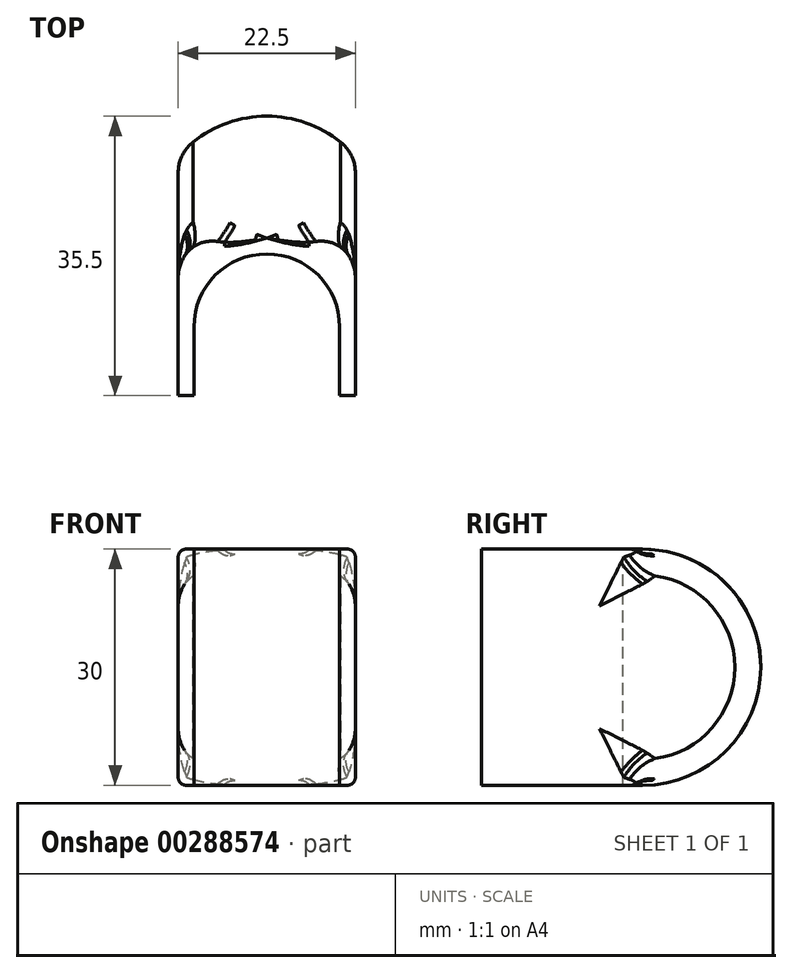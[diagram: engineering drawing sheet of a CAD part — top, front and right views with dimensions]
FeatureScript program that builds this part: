
annotation { "Feature Type Name" : "Feature", "Feature Type Description" : "" }
export const myFeature = defineFeature(function(context is Context, id is Id, definition is map)
    precondition{}
    {
        {
            var Q0;
            Q0=qCreatedBy(makeId("Top.planeOp"),FACE);
            var sketch = newSketch(context, id + "F0", { "sketchPlane" : qUnion([Q0])});
            skLineSegment(sketch, "E0.bottom", {"start": v(11.25, 10) * mm, "end": v(-11.25, 10) * mm});
            skLineSegment(sketch, "E0.top", {"start": v(11.25, -10) * mm, "end": v(-11.25, -10) * mm});
            skLineSegment(sketch, "E0.left", {"start": v(11.25, 10) * mm, "end": v(11.25, -10) * mm});
            skLineSegment(sketch, "E0.right", {"start": v(-11.25, 10) * mm, "end": v(-11.25, -10) * mm});
            skPoint(sketch, "E0.middle", {"position": v(0, 0) * mm});
            skLineSegment(sketch, "E1.bottom", {"start": v(-9.25, -10) * mm, "end": v(9.25, -10) * mm});
            skLineSegment(sketch, "E1.top", {"start": v(-9.25, 8) * mm, "end": v(9.25, 8) * mm});
            skLineSegment(sketch, "E1.left", {"start": v(-9.25, -10) * mm, "end": v(-9.25, 8) * mm});
            skLineSegment(sketch, "E1.right", {"start": v(9.25, -10) * mm, "end": v(9.25, 8) * mm});
            skSolve(sketch);
        }
        {
            var Q0;
            Q0=makeQuery(id+"F0.imprint","IMPRINT",FACE,{"disambiguationData":[TD([[makeQuery(id+"F0.imprint","IMPRINT",EDGE,{"derivedFrom":sQuery(id+"F0.wireOp",EDGE,"E0.bottom")}),1.0]])]});
            extrude(context, id + "F1", {"entities" : qUnion([Q0]), "endBound" : BoundingType.SYMMETRIC, "depth" : 30 * mm, "offsetDistance" : 25 * mm});
        }
        {
            var Q0;
            Q0=makeQuery(id+"F1.opExtrude","SWEPT_FACE",FACE,{"disambiguationData":[OSD([sQuery(id+"F0.wireOp",EDGE,"E0.bottom")])]});
            var sketch = newSketch(context, id + "F2", { "sketchPlane" : qUnion([Q0])});
            skCircle(sketch, "E2", {"center": v(0, 0) * mm, "radius": 15 * mm});
            skSolve(sketch);
        }
        {
            var Q0;
            {var subQ0=sQuery(id+"F2.wireOp",EDGE,"E2");var subQ1=sQuery(id+"F0.wireOp",EDGE,"E0.bottom");var subQ7=makeQuery(id+"F2.imprint","INTERSECT",VERTEX,{"derivedFrom":[makeQuery(id+"F1.opExtrude","CAP_EDGE",EDGE,{"disambiguationData":[OSD([subQ1])],"isStart":false}),subQ0]});Q0=makeQuery(id+"F2.imprint","IMPRINT",FACE,{"disambiguationData":[TD([[makeQuery(id+"F2.imprint","IMPRINT",EDGE,{"disambiguationData":[TD([[subQ7,1.0]])],"derivedFrom":subQ0}),1.0]])]});}
            extrude(context, id + "F3", {"entities" : qUnion([Q0]), "operationType" : NewBodyOperationType.ADD, "depth" : 15.5 * mm, "offsetDistance" : 25 * mm});
        }
        {
            var Q0;
            {var subQ0=sQuery(id+"F2.wireOp",EDGE,"E2");var subQ1=sQuery(id+"F0.wireOp",EDGE,"E0.bottom");var subQ2=makeQuery(id+"F2.imprint","INTERSECT",VERTEX,{"derivedFrom":[makeQuery(id+"F1.opExtrude","CAP_EDGE",EDGE,{"disambiguationData":[OSD([subQ1])],"isStart":false}),subQ0]});Q0=makeQuery(id+"F3.opExtrude","CAP_EDGE",EDGE,{"disambiguationData":[OSD([subQ0]),TDD([makeQuery(id+"F2.imprint","IMPRINT",EDGE,{"disambiguationData":[TD([[subQ2,1.0]])],"derivedFrom":subQ0}),makeQuery(id+"F2.imprint","IMPRINT",EDGE,{"disambiguationData":[TD([[subQ2,-1.0]])],"derivedFrom":subQ0})])],"isStart":false});}
            fillet(context, id + "F4", {"entities" : qUnion([Q0]), "radius" : 15 * mm, "tangentPropagation" : true, "allowEdgeOverflow" : false});
        }
        {
            var Q0;
            Q0=makeQuery(id+"F1.opExtrude","SWEPT_EDGE",EDGE,{"disambiguationData":[OSD([sQuery(id+"F0.wireOp",EDGE,"E1.top"),sQuery(id+"F0.wireOp",EDGE,"E1.left")])]});
            var Q1;
            Q1=makeQuery(id+"F1.opExtrude","SWEPT_EDGE",EDGE,{"disambiguationData":[OSD([sQuery(id+"F0.wireOp",EDGE,"E1.top"),sQuery(id+"F0.wireOp",EDGE,"E1.right")])]});
            fillet(context, id + "F5", {"entities" : qUnion([Q0, Q1]), "radius" : 9.25 * mm, "tangentPropagation" : true, "allowEdgeOverflow" : false});
        }
        {
            var Q0;
            {var subQ0=sQuery(id+"F0.wireOp",EDGE,"E0.right");var subQ1=sQuery(id+"F0.wireOp",EDGE,"E0.bottom");var subQ2=sQuery(id+"F2.wireOp",EDGE,"E2");var subQ3=makeQuery(id+"F2.imprint","INTERSECT",VERTEX,{"derivedFrom":[makeQuery(id+"F1.opExtrude","CAP_EDGE",EDGE,{"disambiguationData":[OSD([subQ1])],"isStart":false}),subQ2]});Q0=makeQuery(id+"F4.opFillet","BLEND_EDGE",EDGE,{"blendedFrom":[makeQuery(id+"F3.opExtrude","CAP_EDGE",EDGE,{"disambiguationData":[OSD([subQ2]),TDD([makeQuery(id+"F2.imprint","IMPRINT",EDGE,{"disambiguationData":[TD([[subQ3,1.0]])],"derivedFrom":subQ2}),makeQuery(id+"F2.imprint","IMPRINT",EDGE,{"disambiguationData":[TD([[subQ3,-1.0]])],"derivedFrom":subQ2})])],"isStart":false}),makeQuery(id+"F3.boolean.opBoolean","MERGE",FACE,{"derivedFrom":[makeQuery(id+"F1.opExtrude","SWEPT_FACE",FACE,{"disambiguationData":[OSD([subQ0])]}),makeQuery(id+"F3.opExtrude","SWEPT_FACE",FACE,{"disambiguationData":[OSD([subQ1,subQ0])]})]})],"blendedInto":[makeQuery(id+"F3.boolean.opBoolean","MERGE",FACE,{"derivedFrom":[makeQuery(id+"F1.opExtrude","SWEPT_FACE",FACE,{"disambiguationData":[OSD([subQ0])]}),makeQuery(id+"F3.opExtrude","SWEPT_FACE",FACE,{"disambiguationData":[OSD([subQ1,subQ0])]})]})]});}
            var Q1;
            {var subQ0=sQuery(id+"F0.wireOp",EDGE,"E0.left");var subQ1=sQuery(id+"F0.wireOp",EDGE,"E0.bottom");var subQ2=sQuery(id+"F2.wireOp",EDGE,"E2");var subQ3=makeQuery(id+"F2.imprint","INTERSECT",VERTEX,{"derivedFrom":[makeQuery(id+"F1.opExtrude","CAP_EDGE",EDGE,{"disambiguationData":[OSD([subQ1])],"isStart":false}),subQ2]});Q1=makeQuery(id+"F4.opFillet","BLEND_EDGE",EDGE,{"blendedFrom":[makeQuery(id+"F3.opExtrude","CAP_EDGE",EDGE,{"disambiguationData":[OSD([subQ2]),TDD([makeQuery(id+"F2.imprint","IMPRINT",EDGE,{"disambiguationData":[TD([[subQ3,1.0]])],"derivedFrom":subQ2}),makeQuery(id+"F2.imprint","IMPRINT",EDGE,{"disambiguationData":[TD([[subQ3,-1.0]])],"derivedFrom":subQ2})])],"isStart":false}),makeQuery(id+"F3.boolean.opBoolean","MERGE",FACE,{"derivedFrom":[makeQuery(id+"F1.opExtrude","SWEPT_FACE",FACE,{"disambiguationData":[OSD([subQ0])]}),makeQuery(id+"F3.opExtrude","SWEPT_FACE",FACE,{"disambiguationData":[OSD([subQ1,subQ0])]})]})],"blendedInto":[makeQuery(id+"F3.boolean.opBoolean","MERGE",FACE,{"derivedFrom":[makeQuery(id+"F1.opExtrude","SWEPT_FACE",FACE,{"disambiguationData":[OSD([subQ0])]}),makeQuery(id+"F3.opExtrude","SWEPT_FACE",FACE,{"disambiguationData":[OSD([subQ1,subQ0])]})]})]});}
            var Q2;
            {var subQ0=sQuery(id+"F2.wireOp",EDGE,"E2");var subQ1=sQuery(id+"F0.wireOp",EDGE,"E0.bottom");var subQ2=makeQuery(id+"F2.imprint","INTERSECT",VERTEX,{"derivedFrom":[makeQuery(id+"F1.opExtrude","CAP_EDGE",EDGE,{"disambiguationData":[OSD([subQ1])],"isStart":true}),subQ0]});var subQ3=sQuery(id+"F0.wireOp",EDGE,"E0.right");var subQ4=makeQuery(id+"F1.opExtrude","SWEPT_EDGE",EDGE,{"disambiguationData":[OSD([subQ1,subQ3])]});Q2=makeQuery(id+"F3.boolean.opBoolean","SPLIT",EDGE,{"disambiguationData":[TD([makeQuery(id+"F3.opExtrude","SWEPT_FACE",FACE,{"disambiguationData":[OSD([subQ0]),TDD([makeQuery(id+"F2.imprint","IMPRINT",EDGE,{"disambiguationData":[TD([[subQ2,1.0]])],"derivedFrom":subQ0}),makeQuery(id+"F2.imprint","IMPRINT",EDGE,{"disambiguationData":[TD([[subQ2,-1.0]])],"derivedFrom":subQ0})])]})])],"derivedFrom":subQ4});}
            var Q3;
            {var subQ0=sQuery(id+"F2.wireOp",EDGE,"E2");var subQ1=sQuery(id+"F0.wireOp",EDGE,"E0.bottom");var subQ2=makeQuery(id+"F2.imprint","INTERSECT",VERTEX,{"derivedFrom":[makeQuery(id+"F1.opExtrude","CAP_EDGE",EDGE,{"disambiguationData":[OSD([subQ1])],"isStart":false}),subQ0]});var subQ4=sQuery(id+"F0.wireOp",EDGE,"E0.right");var subQ5=makeQuery(id+"F1.opExtrude","SWEPT_EDGE",EDGE,{"disambiguationData":[OSD([subQ1,subQ4])]});Q3=makeQuery(id+"F3.boolean.opBoolean","SPLIT",EDGE,{"disambiguationData":[TD([makeQuery(id+"F3.opExtrude","SWEPT_FACE",FACE,{"disambiguationData":[OSD([subQ0]),TDD([makeQuery(id+"F2.imprint","IMPRINT",EDGE,{"disambiguationData":[TD([[subQ2,1.0]])],"derivedFrom":subQ0}),makeQuery(id+"F2.imprint","IMPRINT",EDGE,{"disambiguationData":[TD([[subQ2,-1.0]])],"derivedFrom":subQ0})])]})])],"derivedFrom":subQ5});}
            var Q4;
            {var subQ0=sQuery(id+"F2.wireOp",EDGE,"E2");var subQ1=sQuery(id+"F0.wireOp",EDGE,"E0.bottom");var subQ2=makeQuery(id+"F2.imprint","INTERSECT",VERTEX,{"derivedFrom":[makeQuery(id+"F1.opExtrude","CAP_EDGE",EDGE,{"disambiguationData":[OSD([subQ1])],"isStart":true}),subQ0]});var subQ4=sQuery(id+"F0.wireOp",EDGE,"E0.left");var subQ5=makeQuery(id+"F1.opExtrude","SWEPT_EDGE",EDGE,{"disambiguationData":[OSD([subQ1,subQ4])]});Q4=makeQuery(id+"F3.boolean.opBoolean","SPLIT",EDGE,{"disambiguationData":[TD([makeQuery(id+"F3.opExtrude","SWEPT_FACE",FACE,{"disambiguationData":[OSD([subQ0]),TDD([makeQuery(id+"F2.imprint","IMPRINT",EDGE,{"disambiguationData":[TD([[subQ2,1.0]])],"derivedFrom":subQ0}),makeQuery(id+"F2.imprint","IMPRINT",EDGE,{"disambiguationData":[TD([[subQ2,-1.0]])],"derivedFrom":subQ0})])]})])],"derivedFrom":subQ5});}
            var Q5;
            {var subQ0=sQuery(id+"F2.wireOp",EDGE,"E2");var subQ1=sQuery(id+"F0.wireOp",EDGE,"E0.bottom");var subQ2=makeQuery(id+"F2.imprint","INTERSECT",VERTEX,{"derivedFrom":[makeQuery(id+"F1.opExtrude","CAP_EDGE",EDGE,{"disambiguationData":[OSD([subQ1])],"isStart":false}),subQ0]});var subQ3=sQuery(id+"F0.wireOp",EDGE,"E0.left");var subQ4=makeQuery(id+"F1.opExtrude","SWEPT_EDGE",EDGE,{"disambiguationData":[OSD([subQ1,subQ3])]});Q5=makeQuery(id+"F3.boolean.opBoolean","SPLIT",EDGE,{"disambiguationData":[TD([makeQuery(id+"F3.opExtrude","SWEPT_FACE",FACE,{"disambiguationData":[OSD([subQ0]),TDD([makeQuery(id+"F2.imprint","IMPRINT",EDGE,{"disambiguationData":[TD([[subQ2,1.0]])],"derivedFrom":subQ0}),makeQuery(id+"F2.imprint","IMPRINT",EDGE,{"disambiguationData":[TD([[subQ2,-1.0]])],"derivedFrom":subQ0})])]})])],"derivedFrom":subQ4});}
            fillet(context, id + "F6", {"entities" : qUnion([Q0, Q1, Q2, Q3, Q4, Q5]), "radius" : 5 * mm, "tangentPropagation" : true, "allowEdgeOverflow" : false});
        }
        {
            var Q0;
            {var subQ1=sQuery(id+"F0.wireOp",EDGE,"E0.bottom");var subQ2=makeQuery(id+"F1.opExtrude","CAP_EDGE",EDGE,{"disambiguationData":[OSD([subQ1])],"isStart":false});var subQ5=sQuery(id+"F0.wireOp",EDGE,"E0.right");Q0=makeQuery(id+"F3.boolean.opBoolean","SPLIT",EDGE,{"disambiguationData":[TD([makeQuery(id+"F1.opExtrude","SWEPT_FACE",FACE,{"disambiguationData":[OSD([subQ5])]})])],"derivedFrom":subQ2});}
            var Q1;
            {var subQ1=sQuery(id+"F0.wireOp",EDGE,"E0.bottom");var subQ2=makeQuery(id+"F1.opExtrude","CAP_EDGE",EDGE,{"disambiguationData":[OSD([subQ1])],"isStart":true});var subQ5=sQuery(id+"F0.wireOp",EDGE,"E0.left");Q1=makeQuery(id+"F3.boolean.opBoolean","SPLIT",EDGE,{"disambiguationData":[TD([makeQuery(id+"F1.opExtrude","SWEPT_FACE",FACE,{"disambiguationData":[OSD([subQ5])]})])],"derivedFrom":subQ2});}
            fillet(context, id + "F7", {"entities" : qUnion([Q0, Q1]), "radius" : 1 * mm, "tangentPropagation" : true, "allowEdgeOverflow" : false});
        }
        {
            var Q0;
            {var subQ0=sQuery(id+"F2.wireOp",EDGE,"E2");var subQ1=sQuery(id+"F0.wireOp",EDGE,"E0.bottom");var subQ2=makeQuery(id+"F2.imprint","INTERSECT",VERTEX,{"derivedFrom":[makeQuery(id+"F1.opExtrude","CAP_EDGE",EDGE,{"disambiguationData":[OSD([subQ1])],"isStart":true}),subQ0]});var subQ3=sQuery(id+"F0.wireOp",EDGE,"E0.right");var subQ4=makeQuery(id+"F1.opExtrude","SWEPT_EDGE",EDGE,{"disambiguationData":[OSD([subQ1,subQ3])]});var subQ6=makeQuery(id+"F3.opExtrude","SWEPT_FACE",FACE,{"disambiguationData":[OSD([subQ0]),TDD([makeQuery(id+"F2.imprint","IMPRINT",EDGE,{"disambiguationData":[TD([[subQ2,1.0]])],"derivedFrom":subQ0}),makeQuery(id+"F2.imprint","IMPRINT",EDGE,{"disambiguationData":[TD([[subQ2,-1.0]])],"derivedFrom":subQ0})])]});Q0=makeQuery(id+"F6.opFillet","BLEND_EDGE",EDGE,{"blendedFrom":[makeQuery(id+"F3.boolean.opBoolean","SPLIT",EDGE,{"disambiguationData":[TD([subQ6])],"derivedFrom":subQ4}),subQ6],"blendedInto":[subQ6]});}
            var Q1;
            {var subQ0=sQuery(id+"F2.wireOp",EDGE,"E2");var subQ1=sQuery(id+"F0.wireOp",EDGE,"E0.bottom");var subQ2=makeQuery(id+"F2.imprint","INTERSECT",VERTEX,{"derivedFrom":[makeQuery(id+"F1.opExtrude","CAP_EDGE",EDGE,{"disambiguationData":[OSD([subQ1])],"isStart":true}),subQ0]});var subQ4=sQuery(id+"F0.wireOp",EDGE,"E0.left");var subQ5=makeQuery(id+"F1.opExtrude","SWEPT_EDGE",EDGE,{"disambiguationData":[OSD([subQ1,subQ4])]});var subQ6=makeQuery(id+"F3.opExtrude","SWEPT_FACE",FACE,{"disambiguationData":[OSD([subQ0]),TDD([makeQuery(id+"F2.imprint","IMPRINT",EDGE,{"disambiguationData":[TD([[subQ2,1.0]])],"derivedFrom":subQ0}),makeQuery(id+"F2.imprint","IMPRINT",EDGE,{"disambiguationData":[TD([[subQ2,-1.0]])],"derivedFrom":subQ0})])]});Q1=makeQuery(id+"F6.opFillet","BLEND_EDGE",EDGE,{"blendedFrom":[makeQuery(id+"F3.boolean.opBoolean","SPLIT",EDGE,{"disambiguationData":[TD([subQ6])],"derivedFrom":subQ5}),subQ6],"blendedInto":[subQ6]});}
            var Q2;
            {var subQ0=sQuery(id+"F2.wireOp",EDGE,"E2");var subQ1=sQuery(id+"F0.wireOp",EDGE,"E0.bottom");var subQ2=makeQuery(id+"F2.imprint","INTERSECT",VERTEX,{"derivedFrom":[makeQuery(id+"F1.opExtrude","CAP_EDGE",EDGE,{"disambiguationData":[OSD([subQ1])],"isStart":false}),subQ0]});var subQ3=sQuery(id+"F0.wireOp",EDGE,"E0.left");var subQ4=makeQuery(id+"F1.opExtrude","SWEPT_EDGE",EDGE,{"disambiguationData":[OSD([subQ1,subQ3])]});var subQ6=makeQuery(id+"F3.opExtrude","SWEPT_FACE",FACE,{"disambiguationData":[OSD([subQ0]),TDD([makeQuery(id+"F2.imprint","IMPRINT",EDGE,{"disambiguationData":[TD([[subQ2,1.0]])],"derivedFrom":subQ0}),makeQuery(id+"F2.imprint","IMPRINT",EDGE,{"disambiguationData":[TD([[subQ2,-1.0]])],"derivedFrom":subQ0})])]});Q2=makeQuery(id+"F6.opFillet","BLEND_EDGE",EDGE,{"blendedFrom":[makeQuery(id+"F3.boolean.opBoolean","SPLIT",EDGE,{"disambiguationData":[TD([subQ6])],"derivedFrom":subQ4}),subQ6],"blendedInto":[subQ6]});}
            var Q3;
            {var subQ0=sQuery(id+"F2.wireOp",EDGE,"E2");var subQ1=sQuery(id+"F0.wireOp",EDGE,"E0.bottom");var subQ2=makeQuery(id+"F2.imprint","INTERSECT",VERTEX,{"derivedFrom":[makeQuery(id+"F1.opExtrude","CAP_EDGE",EDGE,{"disambiguationData":[OSD([subQ1])],"isStart":false}),subQ0]});var subQ4=sQuery(id+"F0.wireOp",EDGE,"E0.right");var subQ5=makeQuery(id+"F1.opExtrude","SWEPT_EDGE",EDGE,{"disambiguationData":[OSD([subQ1,subQ4])]});var subQ6=makeQuery(id+"F3.opExtrude","SWEPT_FACE",FACE,{"disambiguationData":[OSD([subQ0]),TDD([makeQuery(id+"F2.imprint","IMPRINT",EDGE,{"disambiguationData":[TD([[subQ2,1.0]])],"derivedFrom":subQ0}),makeQuery(id+"F2.imprint","IMPRINT",EDGE,{"disambiguationData":[TD([[subQ2,-1.0]])],"derivedFrom":subQ0})])]});Q3=makeQuery(id+"F6.opFillet","BLEND_EDGE",EDGE,{"blendedFrom":[makeQuery(id+"F3.boolean.opBoolean","SPLIT",EDGE,{"disambiguationData":[TD([subQ6])],"derivedFrom":subQ5}),subQ6],"blendedInto":[subQ6]});}
            fillet(context, id + "F8", {"entities" : qUnion([Q0, Q1, Q2, Q3]), "radius" : 5 * mm, "tangentPropagation" : true, "allowEdgeOverflow" : false});
        }
    });
